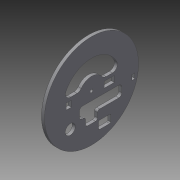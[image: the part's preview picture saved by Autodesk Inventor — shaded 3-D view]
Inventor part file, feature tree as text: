
AUTODESK INVENTOR PART (.ipt)
format: ipt  version: 2015 (Build 190159000, 159)  size: 202,240 bytes
history: native  units: mm
features: extrude x6, sketch x5, fillet x2
ambient origin geometry x8: Origin, YZ Plane, XZ Plane, XY Plane, X Axis, Y Axis, Z Axis, Center Point
bodies: Body1 (feature_tree)
feature tree (13):
  extrude  "Extrusion3"  Depth=28.0mm
  extrude  "Extrusion5"  Depth=3.0mm
  extrude  "Extrusion6"  Depth=3.0mm TaperAngle=0.0deg
  extrude  "Extrusion9"  Depth=5.0mm
  fillet  "Fillet1"  Radius=3.0mm
  extrude  "Extrusion10"  Depth=10.0mm
  fillet  "Fillet2"  Radius=10.0mm
  extrude  "Extrusion11"  Depth=12.5mm
  sketch  "Sketch2"  dims[d0=94.0mm d5=28.0mm]
  sketch  "Sketch4"  dims[d6=25.0mm d7=3.0mm]
  sketch  "Sketch7"  dims[d8=47.0mm d36=3.0mm d37=0.0mm]
  sketch  "Sketch8"  dims[d53=5.0mm d54=5.0mm d55=3.0mm d56=0.0mm]
  sketch  "Sketch9"  dims[d59=5.0mm d60=20.0mm d62=10.0mm d63=12.5mm d64=3.0mm d65=0.0mm d86=12.0mm d90=8.5mm d91=3.0mm d94=6.0mm d95=93.0mm d96=3.0mm d97=42.0mm d98=11.0mm d99=5.0mm d100=3.0mm d101=40.0mm d102=6.0mm d104=2.0mm d105=12.0mm d106=8.5mm d107=10.0mm d108=0.0mm d109=2.0mm d110=12.0mm d111=8.0mm d112=29.0mm d113=7.0mm d114=10.0mm d115=0.0mm d116=1.0mm d117=10.0mm d118=22.5mm d119=21.0mm d120=10.0mm d121=0.0mm]
